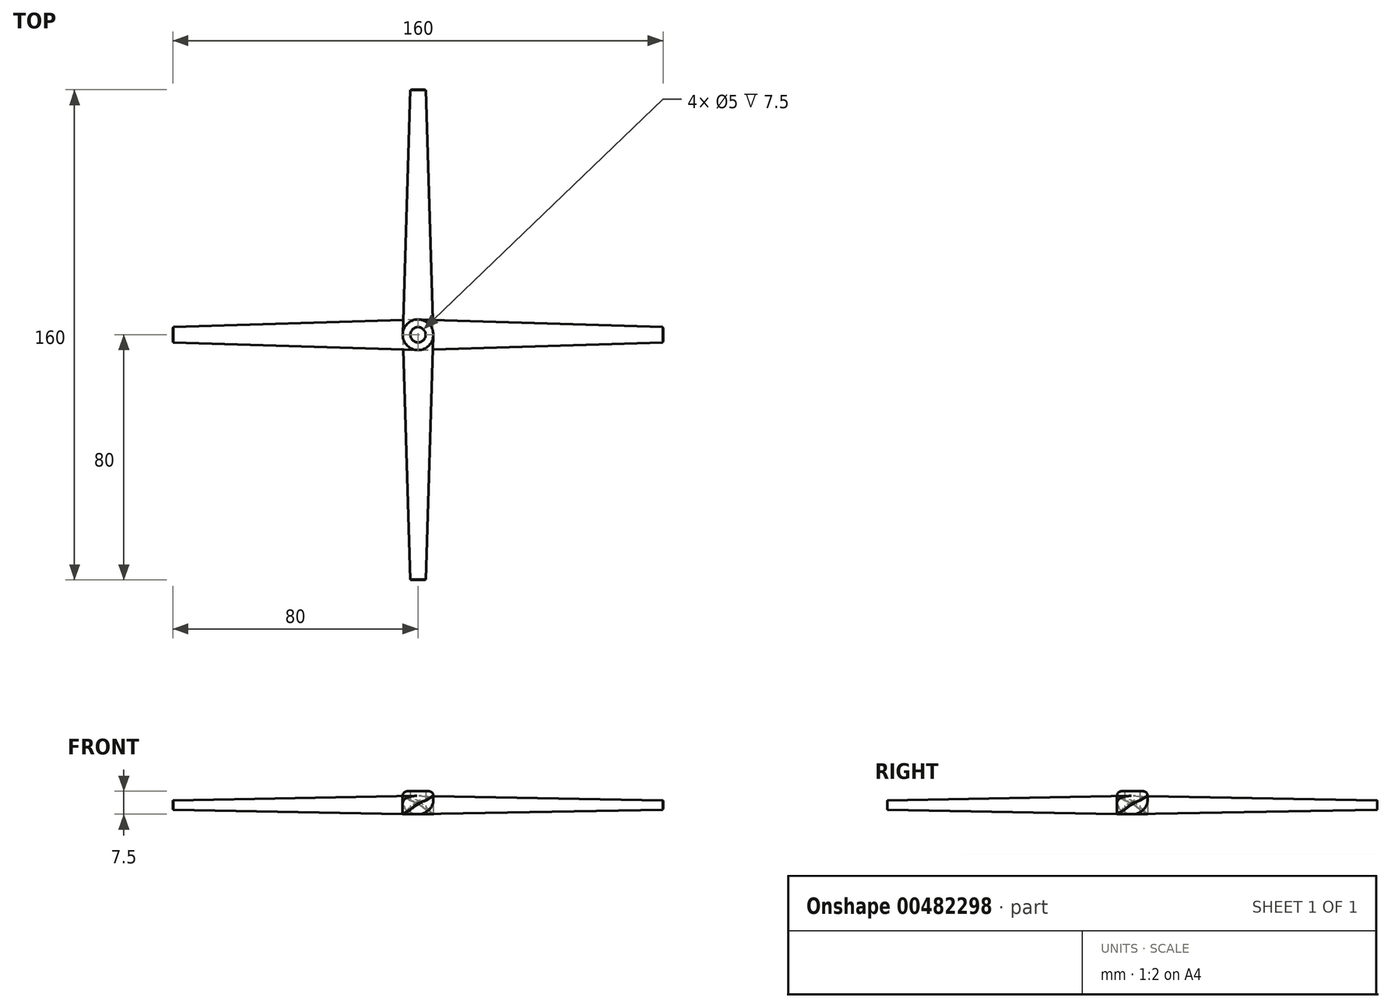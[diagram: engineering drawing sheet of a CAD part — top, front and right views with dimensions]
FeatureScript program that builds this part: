
annotation { "Feature Type Name" : "Feature", "Feature Type Description" : "" }
export const myFeature = defineFeature(function(context is Context, id is Id, definition is map)
    precondition{}
    {
        {
            var Q0;
            Q0=qCreatedBy(makeId("Top.planeOp"),FACE);
            var sketch = newSketch(context, id + "F0", { "sketchPlane" : qUnion([Q0])});
            skCircle(sketch, "E0", {"center": v(0, 0) * mm, "radius": 5 * mm});
            skCircle(sketch, "E1", {"center": v(0, 0) * mm, "radius": 2.5 * mm});
            skSolve(sketch);
        }
        {
            var Q0;
            Q0=makeQuery(id+"F0.imprint","IMPRINT",FACE,{"disambiguationData":[TD([[makeQuery(id+"F0.imprint","IMPRINT",EDGE,{"derivedFrom":sQuery(id+"F0.wireOp",EDGE,"E0")}),1.0]])]});
            extrude(context, id + "F1", {"entities" : qUnion([Q0]), "depth" : 7.5 * mm});
        }
        {
            var Q0;
            Q0=makeQuery(id+"F1.opExtrude","CAP_EDGE",EDGE,{"disambiguationData":[OSD([sQuery(id+"F0.wireOp",EDGE,"E0")])],"isStart":false});
            fillet(context, id + "F2", {"entities" : qUnion([Q0]), "radius" : 1.5 * mm, "tangentPropagation" : true, "allowEdgeOverflow" : false});
        }
        {
            var Q0;
            Q0=qCreatedBy(makeId("Front.planeOp"),FACE);
            var sketch = newSketch(context, id + "F3", { "sketchPlane" : qUnion([Q0])});
            skLineSegment(sketch, "E2", {"start": v(0, 0) * mm, "end": v(-5, 0) * mm, "construction": true});
            skLineSegment(sketch, "E3", {"start": v(-5, 0) * mm, "end": v(5, 0) * mm, "construction": true});
            skLineSegment(sketch, "E4", {"start": v(5, 0) * mm, "end": v(5, 6) * mm, "construction": true});
            skLineSegment(sketch, "E5", {"start": v(0, 0) * mm, "end": v(0, 3.5) * mm, "construction": true});
            skFitSpline(sketch, "E6", {"points": [v(-5, 0) * mm, v(0, 3.5) * mm, v(5, 6) * mm], "startDerivative": vector(9.36, 8.58) * mm, "endDerivative": vector(10.66, 3.35) * mm});
            skLineSegment(sketch, "E7", {"start": v(0, 0) * mm, "end": v(0, 4.34) * mm, "construction": true});
            skPoint(sketch, "E7.endSnap0", {"position": v(0, 1.75) * mm});
            skFitSpline(sketch, "E8", {"points": [v(-5, 0) * mm, v(0, 4.34) * mm, v(5, 6) * mm], "startDerivative": vector(9.16, 9.44) * mm, "endDerivative": vector(10.87, 2.43) * mm});
            skSolve(sketch);
        }
        {
            var Q0;
            Q0=qCreatedBy(makeId("Front.planeOp"),FACE);
            cPlane(context, id + "F4", {"entities" : qUnion([Q0]), "cplaneType" : CPlaneType.OFFSET, "offset" : 80 * mm, "width" : 150 * mm, "height" : 150 * mm});
        }
        {
            var Q0;
            Q0=qCreatedBy(id+"F4.planeOp",FACE);
            var sketch = newSketch(context, id + "F5", { "sketchPlane" : qUnion([Q0])});
            skLineSegment(sketch, "E9", {"start": v(5, 6) * mm, "end": v(5, 4.5) * mm, "construction": true});
            skLineSegment(sketch, "E10", {"start": v(5, 4.5) * mm, "end": v(2.5, 4.5) * mm, "construction": true});
            skFitSpline(sketch, "E11", {"points": [v(-2.5, 1.5) * mm, v(0, 3.5) * mm, v(2.5, 4.5) * mm], "startDerivative": vector(4.68, 4.29) * mm, "endDerivative": vector(5.33, 1.67) * mm});
            skLineSegment(sketch, "E12", {"start": v(-2.5, 1.5) * mm, "end": v(0, 1.5) * mm, "construction": true});
            skLineSegment(sketch, "E13", {"start": v(0, 1.5) * mm, "end": v(0, 3.25) * mm, "construction": true});
            skFitSpline(sketch, "E14", {"points": [v(-2.5, 1.5) * mm, v(0, 3.25) * mm, v(2.5, 4.5) * mm], "startDerivative": vector(4.84, 3.65) * mm, "endDerivative": vector(5.17, 2.34) * mm});
            skSolve(sketch);
        }
        {
            var Q1;
            Q1=makeQuery(id+"F3.imprint","IMPRINT",FACE,{"disambiguationData":[TD([[makeQuery(id+"F3.imprint","IMPRINT",EDGE,{"derivedFrom":sQuery(id+"F3.wireOp",EDGE,"E6")}),1.0]])]});
            var Q2;
            Q2=makeQuery(id+"F5.imprint","IMPRINT",FACE,{"disambiguationData":[TD([[makeQuery(id+"F5.imprint","IMPRINT",EDGE,{"derivedFrom":sQuery(id+"F5.wireOp",EDGE,"E11")}),-1.0]])]});
            loft(context, id + "F6", {"operationType" : NewBodyOperationType.ADD, "sheetProfilesArray" : [{ "sheetProfileEntities" : qUnion([Q1]) }, { "sheetProfileEntities" : qUnion([Q2]) }]});
        }
        {
            var Q0;
            {var subQ0=sQuery(id+"F5.wireOp",EDGE,"E11");var subQ1=sQuery(id+"F5.wireOp",EDGE,"E14");Q0=makeQuery(id+"F6.opLoft","MID_CAP_EDGE",EDGE,{"disambiguationData":[OSD([subQ0,subQ1]),TDD([makeQuery(id+"F5.imprint","INTERSECT",VERTEX,{"disambiguationData":[OD(0.0)],"derivedFrom":[subQ0,subQ1]}),makeQuery(id+"F5.imprint","INTERSECT",VERTEX,{"disambiguationData":[OD(1.0)],"derivedFrom":[subQ0,subQ1]}),makeQuery(id+"F5.imprint","IMPRINT",EDGE,{"derivedFrom":subQ0})])],"capPos":1.0});}
            var Q1;
            {var subQ0=sQuery(id+"F5.wireOp",EDGE,"E14");var subQ1=sQuery(id+"F5.wireOp",EDGE,"E11");Q1=makeQuery(id+"F6.opLoft","MID_CAP_EDGE",EDGE,{"disambiguationData":[OSD([subQ1,subQ0]),TDD([makeQuery(id+"F5.imprint","INTERSECT",VERTEX,{"disambiguationData":[OD(0.0)],"derivedFrom":[subQ1,subQ0]}),makeQuery(id+"F5.imprint","INTERSECT",VERTEX,{"disambiguationData":[OD(1.0)],"derivedFrom":[subQ1,subQ0]}),makeQuery(id+"F5.imprint","IMPRINT",EDGE,{"derivedFrom":subQ0})])],"capPos":1.0});}
            fillet(context, id + "F7", {"entities" : qUnion([Q0, Q1]), "radius" : 0.1 * mm, "tangentPropagation" : true, "allowEdgeOverflow" : false});
        }
        {
            var Q0;
            Q0=makeQuery(id+"F0.imprint","IMPRINT",FACE,{"disambiguationData":[TD([[makeQuery(id+"F0.imprint","IMPRINT",EDGE,{"derivedFrom":sQuery(id+"F0.wireOp",EDGE,"E1")}),1.0]])]});
            extrude(context, id + "F8", {"entities" : qUnion([Q0]), "operationType" : NewBodyOperationType.REMOVE, "depth" : 25 * mm});
        }
        {
            var Q0;
            Q0=makeQuery(id+"F1.opExtrude","SWEPT_BODY",BODY,{"disambiguationData":[OSD([sQuery(id+"F0.wireOp",EDGE,"E0"),sQuery(id+"F0.wireOp",EDGE,"E1")])]});
            var Q1;
            {var subQ0=sQuery(id+"F0.wireOp",EDGE,"E0");Q1=makeQuery(id+"F2.opFillet","BLEND_EDGE",EDGE,{"blendedFrom":[makeQuery(id+"F1.opExtrude","CAP_EDGE",EDGE,{"disambiguationData":[OSD([subQ0])],"isStart":false}),makeQuery(id+"F1.opExtrude","SWEPT_FACE",FACE,{"disambiguationData":[OSD([subQ0])]})],"blendedInto":[makeQuery(id+"F1.opExtrude","SWEPT_FACE",FACE,{"disambiguationData":[OSD([subQ0])]})]});}
            circularPattern(context, id + "F9", {"entities" : qUnion([Q0]), "axis" : qUnion([Q1]), "angle" : 360 * degree, "instanceCount" : 4, "equalSpace" : true});
        }
    });
